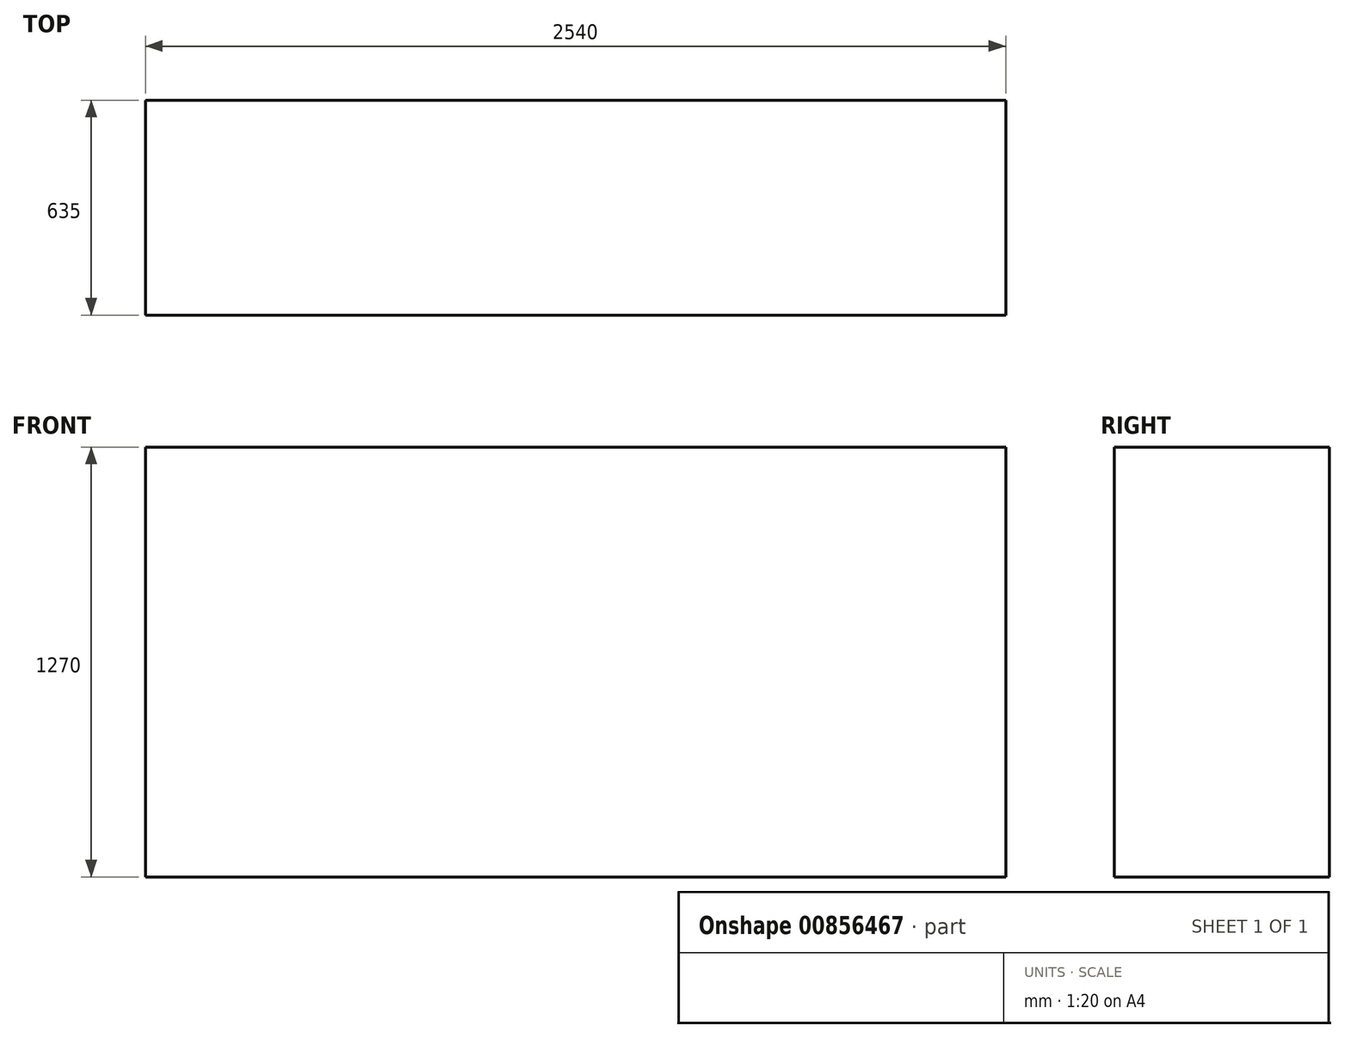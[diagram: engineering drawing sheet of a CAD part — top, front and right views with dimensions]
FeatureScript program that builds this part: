
annotation { "Feature Type Name" : "Feature", "Feature Type Description" : "" }
export const myFeature = defineFeature(function(context is Context, id is Id, definition is map)
    precondition{}
    {
        {
            var Q0;
            Q0=qCreatedBy(makeId("Front.planeOp"),FACE);
            var sketch = newSketch(context, id + "F0", { "sketchPlane" : qUnion([Q0])});
            skLineSegment(sketch, "E0.bottom", {"start": v(0, 0) * mm, "end": v(2540, 0) * mm});
            skLineSegment(sketch, "E0.top", {"start": v(0, 1270) * mm, "end": v(2540, 1270) * mm});
            skLineSegment(sketch, "E0.left", {"start": v(0, 0) * mm, "end": v(0, 1270) * mm});
            skLineSegment(sketch, "E0.right", {"start": v(2540, 0) * mm, "end": v(2540, 1270) * mm});
            skSolve(sketch);
        }
        {
            var Q0;
            Q0 = qSketchRegion(id + "F0", true);
            extrude(context, id + "F1", {"entities" : qUnion([Q0]), "depth" : 635 * mm, "offsetDistance" : 25.4 * mm});
        }
    });
